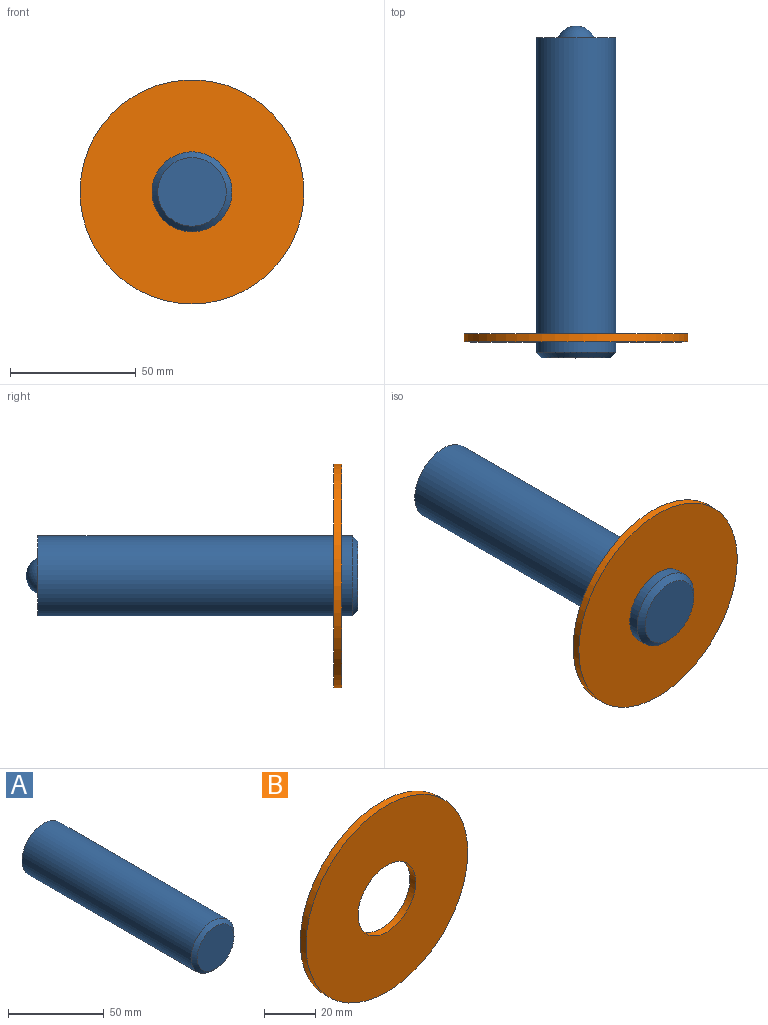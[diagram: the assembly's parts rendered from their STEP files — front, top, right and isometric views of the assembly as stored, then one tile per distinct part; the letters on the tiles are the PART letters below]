
ASSEMBLY  parts=2 mates=2
PART A: 5 faces, bbox 31.8x131.8x31.8 mm
  f0: cylinder r=15.88mm len=124.71mm, axis (0,-1,0), area 12439.7mm2, adj f1,f4
  f1: plane 31.75x31.75mm, normal (0,1,0), area 625.5mm2, adj f0,f3
  f2: plane 27.18x27.18mm, normal (0,-1,0), area 580.1mm2, adj f4
  f3: sphere r=7.94mm, area 237.5mm2, adj f1
  f4: cone r=13.59mm half-angle=45deg, axis (0,1,0), area 299.2mm2, adj f0,f2
PART B: 4 faces, bbox 88.9x3.2x88.9 mm
  f0: cylinder r=44.45mm len=88.9mm, axis (0,1,0), area 886.7mm2, adj f1,f2
  f1: plane 88.9x88.9mm, normal (0,-1,0), area 5415.4mm2, adj f0,f3
  f2: plane 88.9x88.9mm, normal (0,1,0), area 5415.4mm2, adj f0,f3
  f3: cylinder r=15.88mm len=31.75mm, axis (0,-1,0), area 316.7mm2, adj f1,f2
PLACE A at identity
PLACE B t=(-128.15,9.52,0)mm
MATE cylindrical B.f3 <-> A.f0  axis (0,-1,0) through (-128.15,7.94,0)mm
MATE planar B.f0 <-> A.f0  axis (0,-1,0) through (-128.15,6.35,0)mm
